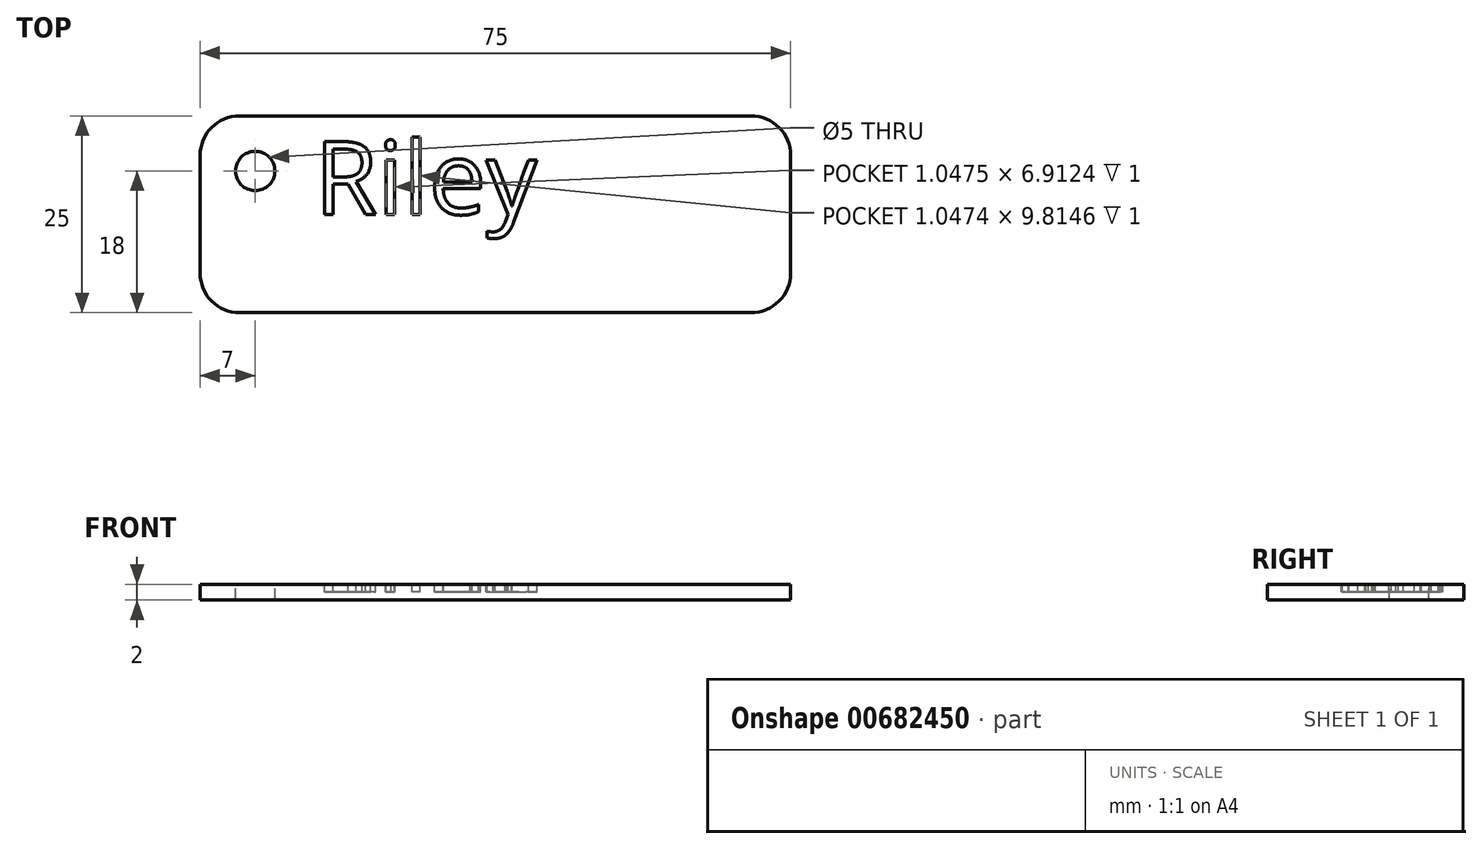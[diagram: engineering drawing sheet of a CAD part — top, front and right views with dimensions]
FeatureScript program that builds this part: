
annotation { "Feature Type Name" : "Feature", "Feature Type Description" : "" }
export const myFeature = defineFeature(function(context is Context, id is Id, definition is map)
    precondition{}
    {
        {
            var Q0;
            Q0=qCreatedBy(makeId("Top.planeOp"),FACE);
            var sketch = newSketch(context, id + "F0", { "sketchPlane" : qUnion([Q0])});
            skLineSegment(sketch, "E0.bottom", {"start": v(32.5, 12.5) * mm, "end": v(-32.5, 12.5) * mm});
            skLineSegment(sketch, "E0.top", {"start": v(32.5, -12.5) * mm, "end": v(-32.5, -12.5) * mm});
            skLineSegment(sketch, "E0.left", {"start": v(37.5, 7.5) * mm, "end": v(37.5, -7.5) * mm});
            skLineSegment(sketch, "E0.right", {"start": v(-37.5, 7.5) * mm, "end": v(-37.5, -7.5) * mm});
            skPoint(sketch, "E0.middle", {"position": v(0, 0) * mm});
            skPoint(sketch, "E1.visualSharp", {"position": v(-37.5, 12.5) * mm});
            skArc(sketch, "E1.filletArc", {"start": v(-32.5, 12.5) * mm, "mid": v(-36.04, 11.04) * mm, "end": v(-37.5, 7.5) * mm});
            skPoint(sketch, "E2.visualSharp", {"position": v(37.5, 12.5) * mm});
            skArc(sketch, "E2.filletArc", {"start": v(37.5, 7.5) * mm, "mid": v(36.04, 11.04) * mm, "end": v(32.5, 12.5) * mm});
            skPoint(sketch, "E3.visualSharp", {"position": v(37.5, -12.5) * mm});
            skArc(sketch, "E3.filletArc", {"start": v(32.5, -12.5) * mm, "mid": v(36.04, -11.04) * mm, "end": v(37.5, -7.5) * mm});
            skPoint(sketch, "E4.visualSharp", {"position": v(-37.5, -12.5) * mm});
            skArc(sketch, "E4.filletArc", {"start": v(-37.5, -7.5) * mm, "mid": v(-36.04, -11.04) * mm, "end": v(-32.5, -12.5) * mm});
            skSolve(sketch);
        }
        {
            var Q0;
            Q0 = qSketchRegion(id + "F0", true);
            extrude(context, id + "F1", {"entities" : qUnion([Q0]), "depth" : 2 * mm, "offsetDistance" : 25 * mm});
        }
        {
            var Q0;
            Q0=makeQuery(id+"F1.opExtrude","CAP_FACE",FACE,{"disambiguationData":[OSD([sQuery(id+"F0.wireOp",EDGE,"E0.bottom"),sQuery(id+"F0.wireOp",EDGE,"E0.top"),sQuery(id+"F0.wireOp",EDGE,"E0.left"),sQuery(id+"F0.wireOp",EDGE,"E0.right"),sQuery(id+"F0.wireOp",EDGE,"E1.filletArc"),sQuery(id+"F0.wireOp",EDGE,"E2.filletArc"),sQuery(id+"F0.wireOp",EDGE,"E3.filletArc"),sQuery(id+"F0.wireOp",EDGE,"E4.filletArc")])],"isStart":false});
            var sketch = newSketch(context, id + "F2", { "sketchPlane" : qUnion([Q0])});
            skPoint(sketch, "E5", {"position": v(-30.5, 5.5) * mm});
            skSolve(sketch);
        }
        {
            var Q0;
            Q0=sQuery(id+"F2.wireOp",VERTEX,"E5");
            var Q1;
            Q1=makeQuery(id+"F1.opExtrude","SWEPT_BODY",BODY,{"disambiguationData":[OSD([sQuery(id+"F0.wireOp",EDGE,"E0.bottom"),sQuery(id+"F0.wireOp",EDGE,"E0.top"),sQuery(id+"F0.wireOp",EDGE,"E0.left"),sQuery(id+"F0.wireOp",EDGE,"E0.right"),sQuery(id+"F0.wireOp",EDGE,"E1.filletArc"),sQuery(id+"F0.wireOp",EDGE,"E2.filletArc"),sQuery(id+"F0.wireOp",EDGE,"E3.filletArc"),sQuery(id+"F0.wireOp",EDGE,"E4.filletArc")])]});
            hole(context, id + "F3", {"style" : HoleStyle.SIMPLE, "endStyle" : HoleEndStyle.THROUGH, "holeDiameter" : 5 * mm, "majorDiameter" : 5 * mm, "isTappedThrough" : true, "tappedDepth" : 12 * mm, "tapClearance" : 3, "locations" : qUnion([Q0]), "scope" : qUnion([Q1])});
        }
        {
            var Q0;
            Q0=makeQuery(id+"F1.opExtrude","CAP_FACE",FACE,{"disambiguationData":[OSD([sQuery(id+"F0.wireOp",EDGE,"E0.bottom"),sQuery(id+"F0.wireOp",EDGE,"E0.top"),sQuery(id+"F0.wireOp",EDGE,"E0.left"),sQuery(id+"F0.wireOp",EDGE,"E0.right"),sQuery(id+"F0.wireOp",EDGE,"E1.filletArc"),sQuery(id+"F0.wireOp",EDGE,"E2.filletArc"),sQuery(id+"F0.wireOp",EDGE,"E3.filletArc"),sQuery(id+"F0.wireOp",EDGE,"E4.filletArc")])],"isStart":false});
            var sketch = newSketch(context, id + "F4", { "sketchPlane" : qUnion([Q0])});
            skText(sketch, "E6", { "text": "Riley", "fontName": "OpenSans-Regular.ttf"});
            const initialGuessF4  = {"E6": [-0.02295, 0, 1, 0, 0.0093]};
            skSetInitialGuess(sketch, initialGuessF4);
            skSolve(sketch);
        }
        {
            var Q0;
            Q0 = qSketchRegion(id + "F4", true);
            extrude(context, id + "F5", {"entities" : qUnion([Q0]), "operationType" : NewBodyOperationType.REMOVE, "oppositeDirection" : true, "depth" : 1 * mm, "offsetDistance" : 25 * mm});
        }
    });
